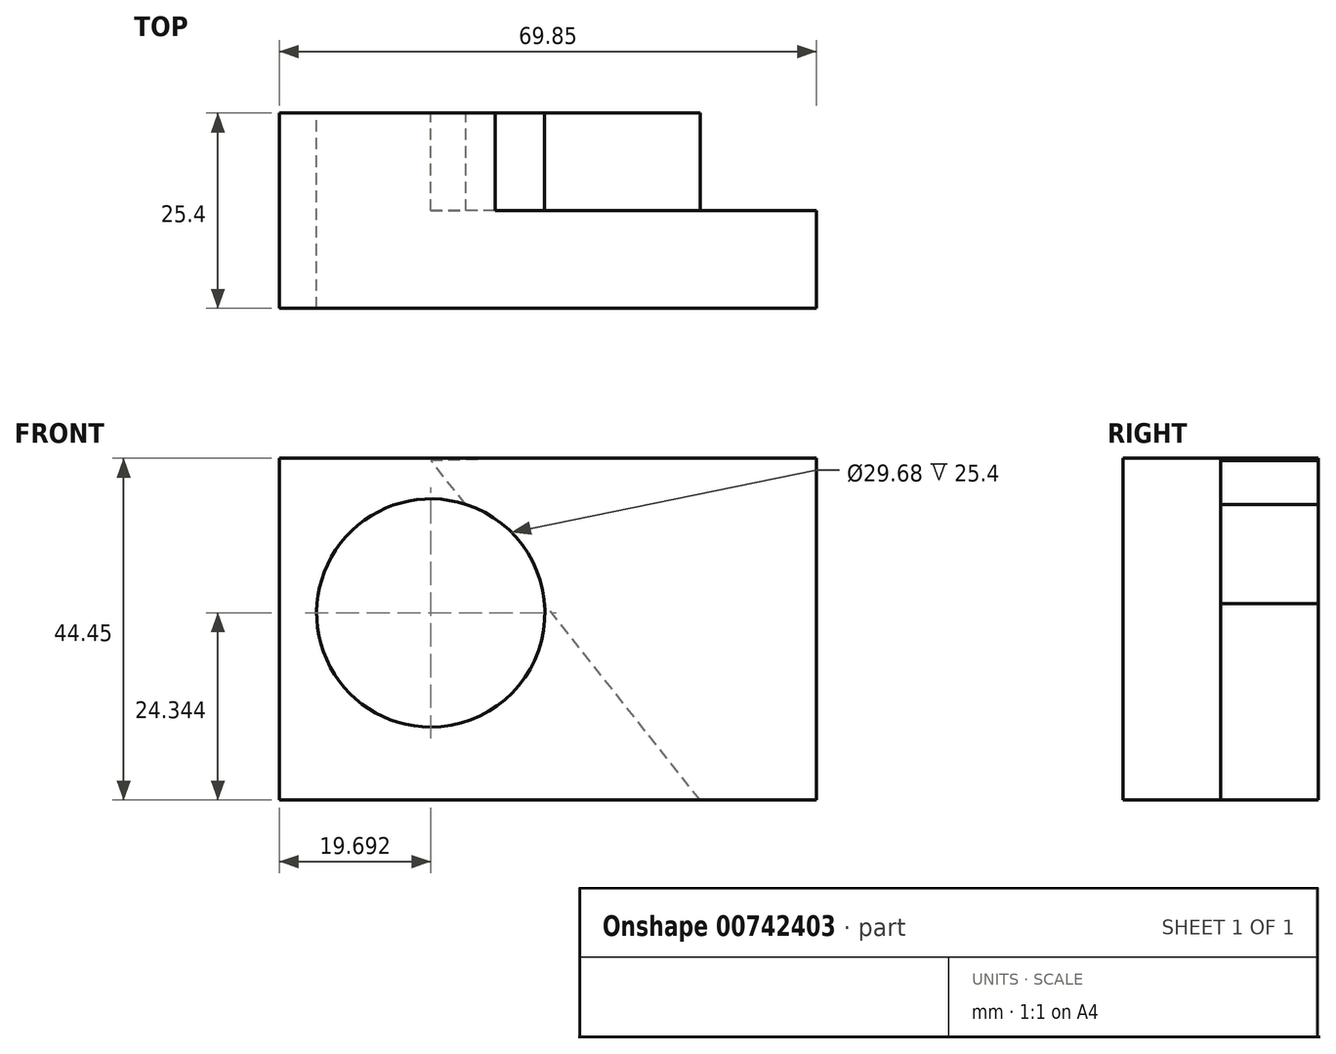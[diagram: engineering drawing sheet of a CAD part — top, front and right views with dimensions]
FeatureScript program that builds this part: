
annotation { "Feature Type Name" : "Feature", "Feature Type Description" : "" }
export const myFeature = defineFeature(function(context is Context, id is Id, definition is map)
    precondition{}
    {
        {
            var Q0;
            Q0=qCreatedBy(makeId("Front.planeOp"),FACE);
            var sketch = newSketch(context, id + "F0", { "sketchPlane" : qUnion([Q0])});
            skLineSegment(sketch, "E0", {"start": v(0, 44.45) * mm, "end": v(0, 0) * mm});
            skLineSegment(sketch, "E1", {"start": v(0, 0) * mm, "end": v(69.85, 0) * mm});
            skLineSegment(sketch, "E2", {"start": v(69.85, 0) * mm, "end": v(69.85, 44.45) * mm});
            skLineSegment(sketch, "E3", {"start": v(69.85, 44.45) * mm, "end": v(0, 44.45) * mm});
            skSolve(sketch);
        }
        {
            var Q0;
            Q0 = qSketchRegion(id + "F0", true);
            extrude(context, id + "F1", {"entities" : qUnion([Q0]), "depth" : 25.4 * mm, "offsetDistance" : 25.4 * mm});
        }
        {
            var Q0;
            Q0=qCreatedBy(makeId("Front.planeOp"),FACE);
            var sketch = newSketch(context, id + "F2", { "sketchPlane" : qUnion([Q0])});
            skLineSegment(sketch, "E4", {"start": v(19.7, 44.2) * mm, "end": v(54.74, 0) * mm});
            skLineSegment(sketch, "E5", {"start": v(54.74, 0) * mm, "end": v(69.93, 0) * mm});
            skLineSegment(sketch, "E6", {"start": v(69.93, 0) * mm, "end": v(69.93, 45.74) * mm});
            skLineSegment(sketch, "E7", {"start": v(69.93, 45.74) * mm, "end": v(19.7, 44.2) * mm});
            skSolve(sketch);
        }
        {
            var Q0;
            Q0 = qSketchRegion(id + "F2", true);
            extrude(context, id + "F3", {"entities" : qUnion([Q0]), "operationType" : NewBodyOperationType.REMOVE, "endBound" : BoundingType.SYMMETRIC, "depth" : 25.4 * mm, "offsetDistance" : 25.4 * mm});
        }
        {
            var Q0;
            Q0=qCreatedBy(makeId("Front.planeOp"),FACE);
            var sketch = newSketch(context, id + "F4", { "sketchPlane" : qUnion([Q0])});
            skCircle(sketch, "E8", {"center": v(19.7, 24.34) * mm, "radius": 14.84 * mm});
            skSolve(sketch);
        }
        {
            var Q0;
            Q0 = qSketchRegion(id + "F4", true);
            extrude(context, id + "F5", {"entities" : qUnion([Q0]), "operationType" : NewBodyOperationType.REMOVE, "endBound" : BoundingType.THROUGH_ALL, "depth" : 25.4 * mm, "offsetDistance" : 25.4 * mm});
        }
    });
